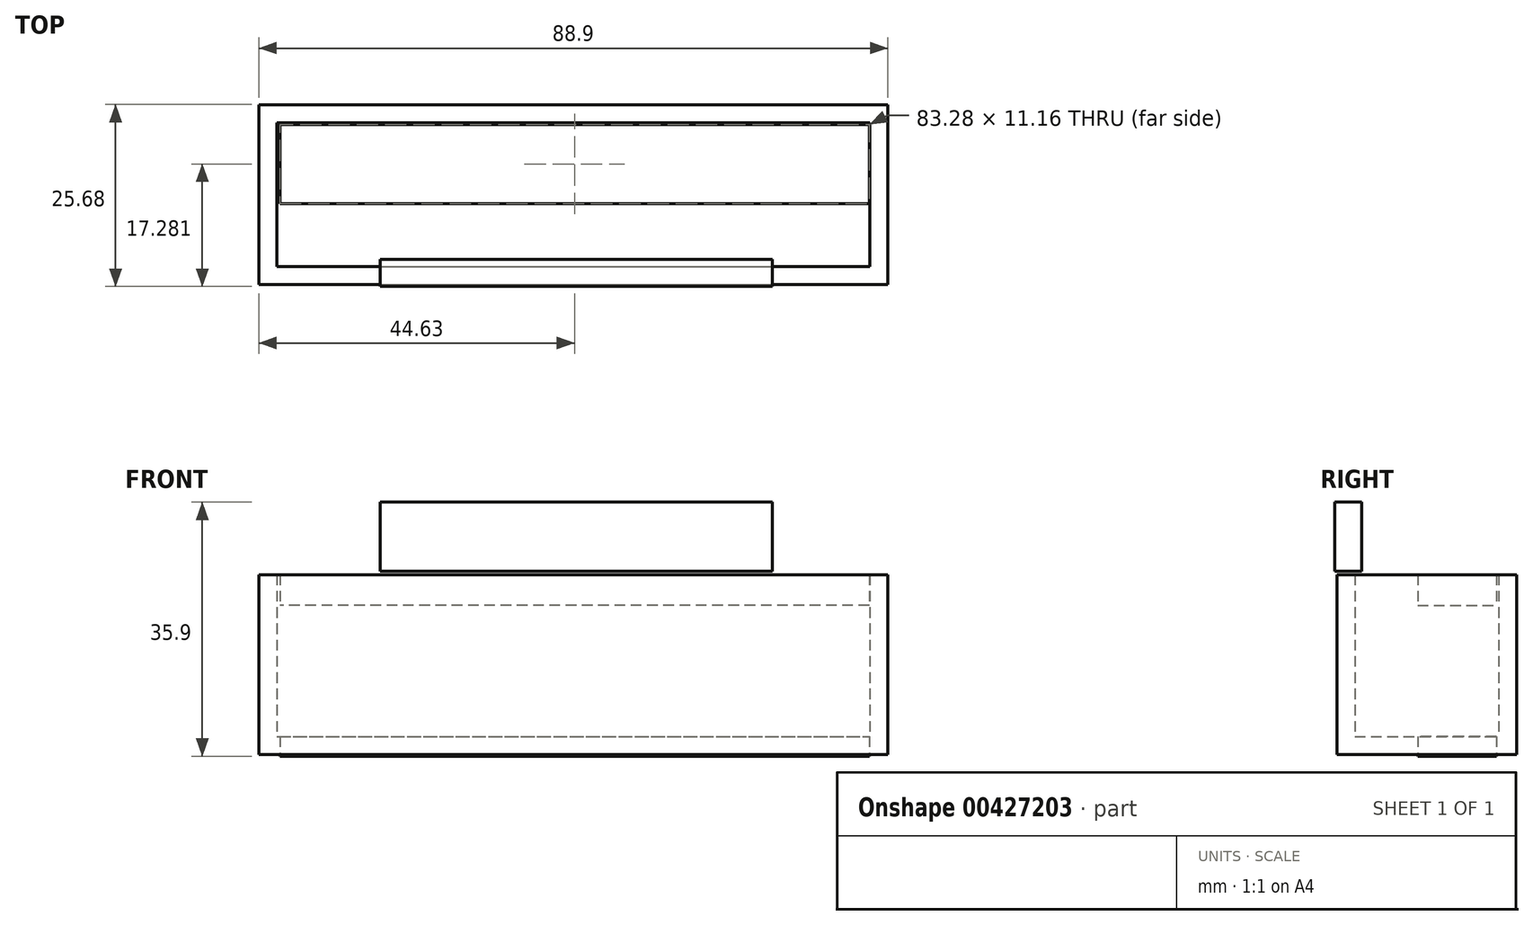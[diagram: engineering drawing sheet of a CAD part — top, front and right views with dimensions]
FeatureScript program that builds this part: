
annotation { "Feature Type Name" : "Feature", "Feature Type Description" : "" }
export const myFeature = defineFeature(function(context is Context, id is Id, definition is map)
    precondition{}
    {
        {
            var Q0;
            Q0=qCreatedBy(makeId("Top.planeOp"),FACE);
            var sketch = newSketch(context, id + "F0", { "sketchPlane" : qUnion([Q0])});
            skLineSegment(sketch, "E0.bottom", {"start": v(-40.82, -3.53) * mm, "end": v(48.08, -3.53) * mm});
            skLineSegment(sketch, "E0.top", {"start": v(-40.82, 21.87) * mm, "end": v(48.08, 21.87) * mm});
            skLineSegment(sketch, "E0.left", {"start": v(-40.82, -3.53) * mm, "end": v(-40.82, 21.87) * mm});
            skLineSegment(sketch, "E0.right", {"start": v(48.08, -3.53) * mm, "end": v(48.08, 21.87) * mm});
            skSolve(sketch);
        }
        {
            var Q0;
            Q0=makeQuery(id+"F0.imprint","IMPRINT",FACE,{"disambiguationData":[TD([[makeQuery(id+"F0.imprint","IMPRINT",EDGE,{"derivedFrom":sQuery(id+"F0.wireOp",EDGE,"E0.bottom")}),1.0]])]});
            extrude(context, id + "F1", {"entities" : qUnion([Q0]), "depth" : 25.4 * mm});
        }
        {
            var Q0;
            Q0=qCreatedBy(makeId("Front.planeOp"),FACE);
            var sketch = newSketch(context, id + "F2", { "sketchPlane" : qUnion([Q0])});
            skLineSegment(sketch, "E1.bottom", {"start": v(-23.68, 35.65) * mm, "end": v(19.6, 35.65) * mm});
            skLineSegment(sketch, "E1.top", {"start": v(-23.68, 25.85) * mm, "end": v(19.6, 25.85) * mm});
            skLineSegment(sketch, "E1.left", {"start": v(-23.68, 35.65) * mm, "end": v(-23.68, 25.85) * mm});
            skLineSegment(sketch, "E1.right", {"start": v(19.6, 35.65) * mm, "end": v(19.6, 25.85) * mm});
            skSolve(sketch);
        }
        {
            var Q0;
            Q0=makeQuery(id+"F2.imprint","IMPRINT",FACE,{"disambiguationData":[TD([[makeQuery(id+"F2.imprint","IMPRINT",EDGE,{"derivedFrom":sQuery(id+"F2.wireOp",EDGE,"E1.bottom")}),-1.0]])]});
            extrude(context, id + "F3", {"entities" : qUnion([Q0]), "depth" : 3.8 * mm});
        }
        {
            var Q0;
            Q0=makeQuery(id+"F3.opExtrude","SWEPT_FACE",FACE,{"disambiguationData":[OSD([sQuery(id+"F2.wireOp",EDGE,"E1.right")])]});
            extrude(context, id + "F4", {"entities" : qUnion([Q0]), "operationType" : NewBodyOperationType.ADD, "depth" : 12.2 * mm});
        }
        {
            var Q0;
            Q0=makeQuery(id+"F1.opExtrude","CAP_FACE",FACE,{"disambiguationData":[OSD([sQuery(id+"F0.wireOp",EDGE,"E0.bottom"),sQuery(id+"F0.wireOp",EDGE,"E0.top"),sQuery(id+"F0.wireOp",EDGE,"E0.left"),sQuery(id+"F0.wireOp",EDGE,"E0.right")])],"isStart":false});
            shell(context, id + "F5", {"entities" : qUnion([Q0]), "thickness" : 2.54 * mm});
        }
        {
            var Q0;
            Q0=qCreatedBy(makeId("Top.planeOp"),FACE);
            var sketch = newSketch(context, id + "F6", { "sketchPlane" : qUnion([Q0])});
            skLineSegment(sketch, "E2.bottom", {"start": v(45.45, 7.9) * mm, "end": v(-37.83, 7.9) * mm});
            skLineSegment(sketch, "E2.top", {"start": v(45.45, 19.05) * mm, "end": v(-37.83, 19.05) * mm});
            skLineSegment(sketch, "E2.left", {"start": v(45.45, 7.9) * mm, "end": v(45.45, 19.05) * mm});
            skLineSegment(sketch, "E2.right", {"start": v(-37.83, 7.9) * mm, "end": v(-37.83, 19.05) * mm});
            skSolve(sketch);
        }
        {
            var Q0;
            Q0 = qSketchRegion(id + "F6", true);
            extrude(context, id + "F7", {"entities" : qUnion([Q0]), "operationType" : NewBodyOperationType.ADD, "depth" : 25.4 * mm});
        }
        {
            var Q0;
            Q0=makeQuery(id+"F6.imprint","IMPRINT",FACE,{"disambiguationData":[TD([[makeQuery(id+"F6.imprint","IMPRINT",EDGE,{"derivedFrom":sQuery(id+"F6.wireOp",EDGE,"E2.bottom")}),-1.0]])]});
            var sketch = newSketch(context, id + "F8", { "sketchPlane" : qUnion([Q0])});
            skLineSegment(sketch, "E3.bottom", {"start": v(-37.83, 7.9) * mm, "end": v(45.45, 7.9) * mm});
            skLineSegment(sketch, "E3.top", {"start": v(-37.83, 19.05) * mm, "end": v(45.45, 19.05) * mm});
            skLineSegment(sketch, "E3.left", {"start": v(-37.83, 7.9) * mm, "end": v(-37.83, 19.05) * mm});
            skLineSegment(sketch, "E3.right", {"start": v(45.45, 7.9) * mm, "end": v(45.45, 19.05) * mm});
            skSolve(sketch);
        }
        {
            var Q0;
            Q0 = qSketchRegion(id + "F8", true);
            extrude(context, id + "F9", {"entities" : qUnion([Q0]), "operationType" : NewBodyOperationType.REMOVE, "depth" : 21.08 * mm});
        }
        {
            var Q0;
            Q0=qCreatedBy(makeId("Top.planeOp"),FACE);
            var sketch = newSketch(context, id + "F10", { "sketchPlane" : qUnion([Q0])});
            skLineSegment(sketch, "E4.bottom", {"start": v(-37.83, 7.9) * mm, "end": v(45.45, 7.9) * mm});
            skLineSegment(sketch, "E4.top", {"start": v(-37.83, 19.05) * mm, "end": v(45.45, 19.05) * mm});
            skLineSegment(sketch, "E4.left", {"start": v(-37.83, 7.9) * mm, "end": v(-37.83, 19.05) * mm});
            skLineSegment(sketch, "E4.right", {"start": v(45.45, 7.9) * mm, "end": v(45.45, 19.05) * mm});
            skSolve(sketch);
        }
        {
            var Q0;
            Q0 = qSketchRegion(id + "F10", true);
            extrude(context, id + "F11", {"entities" : qUnion([Q0]), "oppositeDirection" : true, "depth" : 0.25 * mm});
        }
    });
